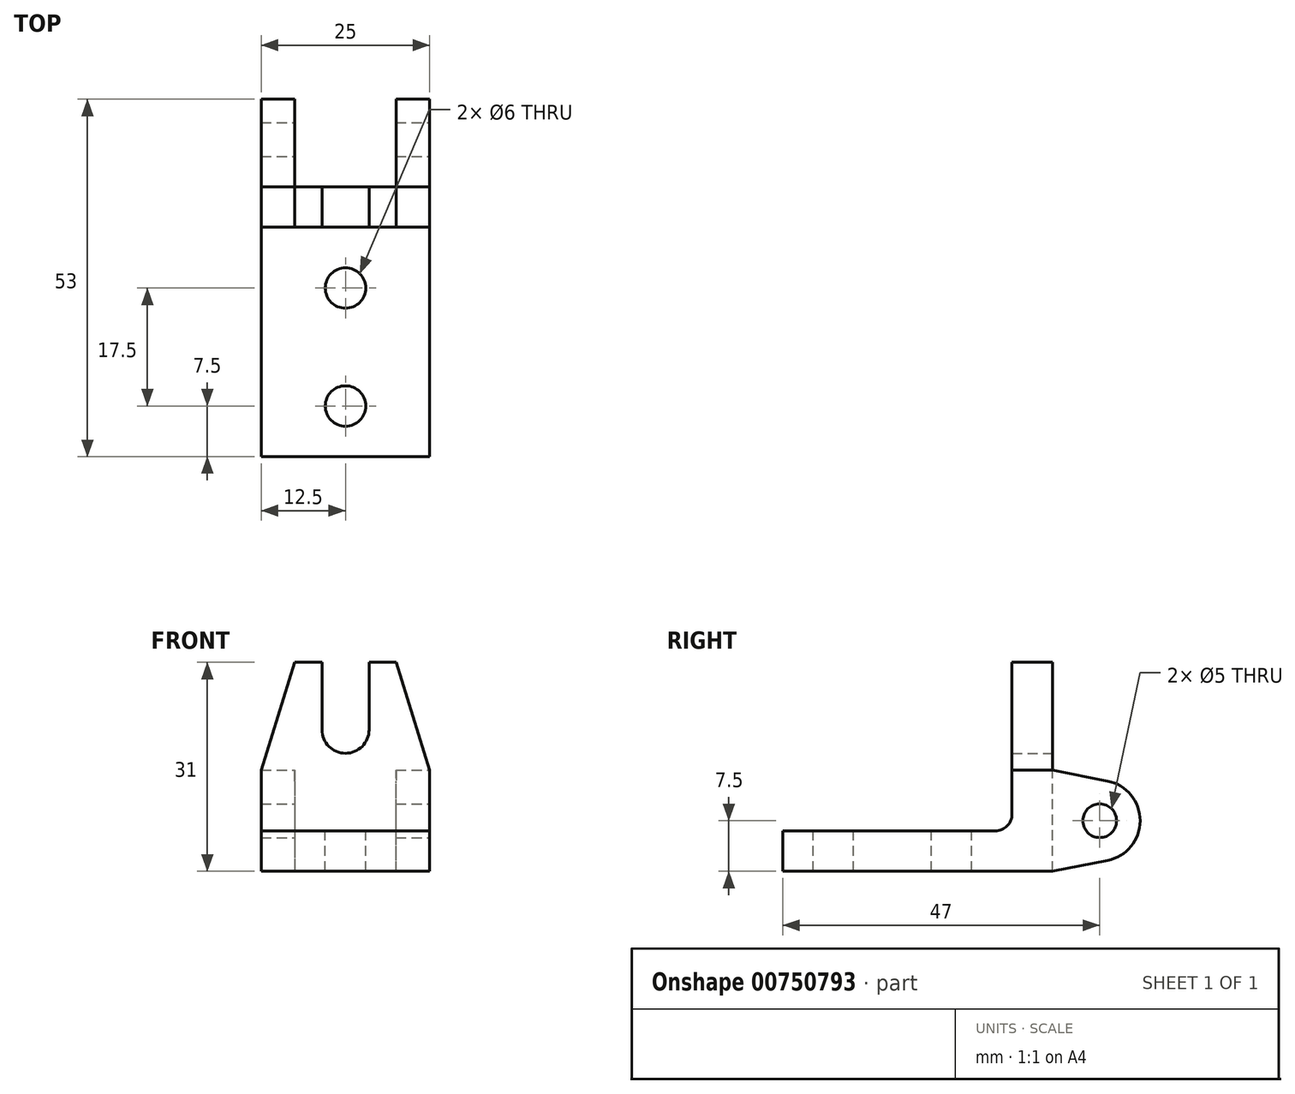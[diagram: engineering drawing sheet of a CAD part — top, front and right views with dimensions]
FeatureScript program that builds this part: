
annotation { "Feature Type Name" : "Feature", "Feature Type Description" : "" }
export const myFeature = defineFeature(function(context is Context, id is Id, definition is map)
    precondition{}
    {
        {
            var Q0;
            Q0=qCreatedBy(makeId("Right.planeOp"),FACE);
            var sketch = newSketch(context, id + "F0", { "sketchPlane" : qUnion([Q0])});
            skLineSegment(sketch, "E0", {"start": v(0, 0) * mm, "end": v(0, 6) * mm});
            skLineSegment(sketch, "E1", {"start": v(0, 0) * mm, "end": v(40, 0) * mm});
            skLineSegment(sketch, "E2", {"start": v(40, 0) * mm, "end": v(40, 31) * mm});
            skLineSegment(sketch, "E3", {"start": v(40, 31) * mm, "end": v(34, 31) * mm});
            skLineSegment(sketch, "E4", {"start": v(34, 31) * mm, "end": v(34, 8.5) * mm});
            skLineSegment(sketch, "E5", {"start": v(31.5, 6) * mm, "end": v(0, 6) * mm});
            skPoint(sketch, "E6.visualSharp", {"position": v(34, 6) * mm});
            skArc(sketch, "E6.filletArc", {"start": v(31.5, 6) * mm, "mid": v(33.27, 6.73) * mm, "end": v(34, 8.5) * mm});
            skSolve(sketch);
        }
        {
            var Q0;
            Q0=makeQuery(id+"F0.imprint","IMPRINT",FACE,{"disambiguationData":[TD([[makeQuery(id+"F0.imprint","IMPRINT",EDGE,{"derivedFrom":sQuery(id+"F0.wireOp",EDGE,"E0")}),-1.0]])]});
            extrude(context, id + "F1", {"entities" : qUnion([Q0]), "depth" : 25 * mm, "offsetDistance" : 25 * mm});
        }
        {
            var Q0;
            Q0=makeQuery(id+"F1.opExtrude","SWEPT_FACE",FACE,{"disambiguationData":[OSD([sQuery(id+"F0.wireOp",EDGE,"E2")])]});
            var sketch = newSketch(context, id + "F2", { "sketchPlane" : qUnion([Q0])});
            skLineSegment(sketch, "E7", {"start": v(0, 0) * mm, "end": v(0, 15) * mm});
            skLineSegment(sketch, "E8", {"start": v(-12.5, 31) * mm, "end": v(-9, 31) * mm});
            skLineSegment(sketch, "E9", {"start": v(-12.5, 31) * mm, "end": v(-16, 31) * mm});
            skLineSegment(sketch, "E10", {"start": v(-12.5, 31) * mm, "end": v(-5, 31) * mm});
            skLineSegment(sketch, "E11", {"start": v(-16, 31) * mm, "end": v(-20, 31) * mm});
            skLineSegment(sketch, "E12", {"start": v(-5, 31) * mm, "end": v(0, 15) * mm});
            skLineSegment(sketch, "E13", {"start": v(-20, 31) * mm, "end": v(-25, 15) * mm});
            skPoint(sketch, "E13.endSnap0", {"position": v(-25, 15.5) * mm});
            skLineSegment(sketch, "E14", {"start": v(-16, 31) * mm, "end": v(-16, 21) * mm});
            skLineSegment(sketch, "E15", {"start": v(-9, 31) * mm, "end": v(-9, 21) * mm});
            skArc(sketch, "E16", {"start": v(-16, 21) * mm, "mid": v(-12.5, 17.5) * mm, "end": v(-9, 21) * mm});
            skLineSegment(sketch, "E17", {"start": v(-25, 15) * mm, "end": v(-25, 32) * mm});
            skLineSegment(sketch, "E18", {"start": v(-25, 32) * mm, "end": v(0, 32) * mm});
            skLineSegment(sketch, "E19", {"start": v(0, 32) * mm, "end": v(0, 15) * mm});
            skSolve(sketch);
        }
        {
            var Q0;
            {var subQ0=sQuery(id+"F2.wireOp",EDGE,"E13");Q0=makeQuery(id+"F2.imprint","IMPRINT",FACE,{"disambiguationData":[TD([[makeQuery(id+"F2.imprint","IMPRINT",EDGE,{"derivedFrom":subQ0}),-1.0]])]});}
            var Q1;
            {var subQ5=sQuery(id+"F2.wireOp",EDGE,"E9");Q1=makeQuery(id+"F2.imprint","IMPRINT",FACE,{"disambiguationData":[TD([[makeQuery(id+"F2.imprint","IMPRINT",EDGE,{"derivedFrom":subQ5}),1.0]])]});}
            var Q2;
            {var subQ0=sQuery(id+"F2.wireOp",EDGE,"E12");Q2=makeQuery(id+"F2.imprint","IMPRINT",FACE,{"disambiguationData":[TD([[makeQuery(id+"F2.imprint","IMPRINT",EDGE,{"derivedFrom":subQ0}),1.0]])]});}
            var Q3;
            {var subQ2=sQuery(id+"F2.wireOp",EDGE,"E9");Q3=makeQuery(id+"F2.imprint","IMPRINT",FACE,{"disambiguationData":[TD([[makeQuery(id+"F2.imprint","IMPRINT",EDGE,{"derivedFrom":subQ2}),-1.0]])]});}
            extrude(context, id + "F3", {"entities" : qUnion([Q0, Q1, Q2, Q3]), "operationType" : NewBodyOperationType.REMOVE, "oppositeDirection" : true, "depth" : 6 * mm, "offsetDistance" : 25 * mm});
        }
        {
            var Q0;
            Q0=makeQuery(id+"F1.opExtrude","SWEPT_FACE",FACE,{"disambiguationData":[OSD([sQuery(id+"F0.wireOp",EDGE,"E5")])]});
            var sketch = newSketch(context, id + "F4", { "sketchPlane" : qUnion([Q0])});
            skCircle(sketch, "E20", {"center": v(12.5, 7.5) * mm, "radius": 3 * mm});
            skCircle(sketch, "E21", {"center": v(12.5, 25) * mm, "radius": 3 * mm});
            skSolve(sketch);
        }
        {
            var Q0;
            Q0=makeQuery(id+"F4.imprint","IMPRINT",FACE,{"disambiguationData":[TD([[makeQuery(id+"F4.imprint","IMPRINT",EDGE,{"derivedFrom":sQuery(id+"F4.wireOp",EDGE,"E21")}),1.0]])]});
            var Q1;
            Q1=makeQuery(id+"F4.imprint","IMPRINT",FACE,{"disambiguationData":[TD([[makeQuery(id+"F4.imprint","IMPRINT",EDGE,{"derivedFrom":sQuery(id+"F4.wireOp",EDGE,"E20")}),1.0]])]});
            extrude(context, id + "F5", {"entities" : qUnion([Q0, Q1]), "operationType" : NewBodyOperationType.REMOVE, "oppositeDirection" : true, "depth" : 6 * mm, "offsetDistance" : 25 * mm});
        }
        {
            var Q0;
            Q0=makeQuery(id+"F1.opExtrude","SWEPT_FACE",FACE,{"disambiguationData":[OSD([sQuery(id+"F0.wireOp",EDGE,"E2")])]});
            var sketch = newSketch(context, id + "F6", { "sketchPlane" : qUnion([Q0])});
            skLineSegment(sketch, "E22", {"start": v(-25, 0) * mm, "end": v(-20, 0) * mm});
            skLineSegment(sketch, "E23", {"start": v(-20, 0) * mm, "end": v(-20, 15) * mm});
            skLineSegment(sketch, "E24", {"start": v(-20, 15) * mm, "end": v(-25, 15) * mm});
            skLineSegment(sketch, "E25", {"start": v(-25, 15) * mm, "end": v(-25, 0) * mm});
            skLineSegment(sketch, "E26", {"start": v(0, 0) * mm, "end": v(0, 15) * mm});
            skLineSegment(sketch, "E27", {"start": v(0, 15) * mm, "end": v(-5, 15) * mm});
            skLineSegment(sketch, "E28", {"start": v(-5, 15) * mm, "end": v(-5, 0) * mm});
            skLineSegment(sketch, "E29", {"start": v(-5, 0) * mm, "end": v(0, 0) * mm});
            skSolve(sketch);
        }
        {
            var Q0;
            Q0=makeQuery(id+"F6.imprint","IMPRINT",FACE,{"disambiguationData":[TD([[makeQuery(id+"F6.imprint","IMPRINT",EDGE,{"derivedFrom":sQuery(id+"F6.wireOp",EDGE,"E22")}),1.0]])]});
            var Q1;
            Q1=makeQuery(id+"F6.imprint","IMPRINT",FACE,{"disambiguationData":[TD([[makeQuery(id+"F6.imprint","IMPRINT",EDGE,{"derivedFrom":sQuery(id+"F6.wireOp",EDGE,"E26")}),1.0]])]});
            extrude(context, id + "F7", {"entities" : qUnion([Q0, Q1]), "operationType" : NewBodyOperationType.ADD, "depth" : 13 * mm, "offsetDistance" : 25 * mm});
        }
        {
            var Q0;
            Q0=makeQuery(id+"F7.boolean.opBoolean","MERGE",FACE,{"derivedFrom":[makeQuery(id+"F1.opExtrude","CAP_FACE",FACE,{"disambiguationData":[OSD([sQuery(id+"F0.wireOp",EDGE,"E0"),sQuery(id+"F0.wireOp",EDGE,"E1"),sQuery(id+"F0.wireOp",EDGE,"E2"),sQuery(id+"F0.wireOp",EDGE,"E3"),sQuery(id+"F0.wireOp",EDGE,"E4"),sQuery(id+"F0.wireOp",EDGE,"E5"),sQuery(id+"F0.wireOp",EDGE,"E6.filletArc")])],"isStart":false}),makeQuery(id+"F7.opExtrude","SWEPT_FACE",FACE,{"disambiguationData":[OSD([sQuery(id+"F6.wireOp",EDGE,"E25")])]})]});
            var sketch = newSketch(context, id + "F8", { "sketchPlane" : qUnion([Q0])});
            skLineSegment(sketch, "E30", {"start": v(40, 0) * mm, "end": v(47, 0) * mm});
            skCircle(sketch, "E31", {"center": v(47, 7.5) * mm, "radius": 2.5 * mm});
            skLineSegment(sketch, "E32", {"start": v(40, 15) * mm, "end": v(48.16, 13.39) * mm});
            skLineSegment(sketch, "E33", {"start": v(40, 0) * mm, "end": v(48.16, 1.61) * mm});
            skArc(sketch, "E34", {"start": v(48.16, 1.61) * mm, "mid": v(53, 7.5) * mm, "end": v(48.16, 13.39) * mm});
            skLineSegment(sketch, "E35", {"start": v(40, 15) * mm, "end": v(53, 15) * mm});
            skLineSegment(sketch, "E36", {"start": v(53, 15) * mm, "end": v(53, 0) * mm});
            skLineSegment(sketch, "E37", {"start": v(53, 0) * mm, "end": v(40, 0) * mm});
            skSolve(sketch);
        }
        {
            var Q0;
            {var subQ0=sQuery(id+"F8.wireOp",EDGE,"E32");Q0=makeQuery(id+"F8.imprint","IMPRINT",FACE,{"disambiguationData":[TD([[makeQuery(id+"F8.imprint","IMPRINT",EDGE,{"derivedFrom":subQ0}),1.0]])]});}
            var Q1;
            Q1=makeQuery(id+"F8.imprint","IMPRINT",FACE,{"disambiguationData":[TD([[makeQuery(id+"F8.imprint","IMPRINT",EDGE,{"derivedFrom":sQuery(id+"F8.wireOp",EDGE,"E31")}),1.0]])]});
            var Q2;
            {var subQ0=sQuery(id+"F8.wireOp",EDGE,"E33");Q2=makeQuery(id+"F8.imprint","IMPRINT",FACE,{"disambiguationData":[TD([[makeQuery(id+"F8.imprint","IMPRINT",EDGE,{"derivedFrom":subQ0}),-1.0]])]});}
            extrude(context, id + "F9", {"entities" : qUnion([Q0, Q1, Q2]), "operationType" : NewBodyOperationType.REMOVE, "oppositeDirection" : true, "depth" : 25 * mm, "offsetDistance" : 25 * mm});
        }
    });
